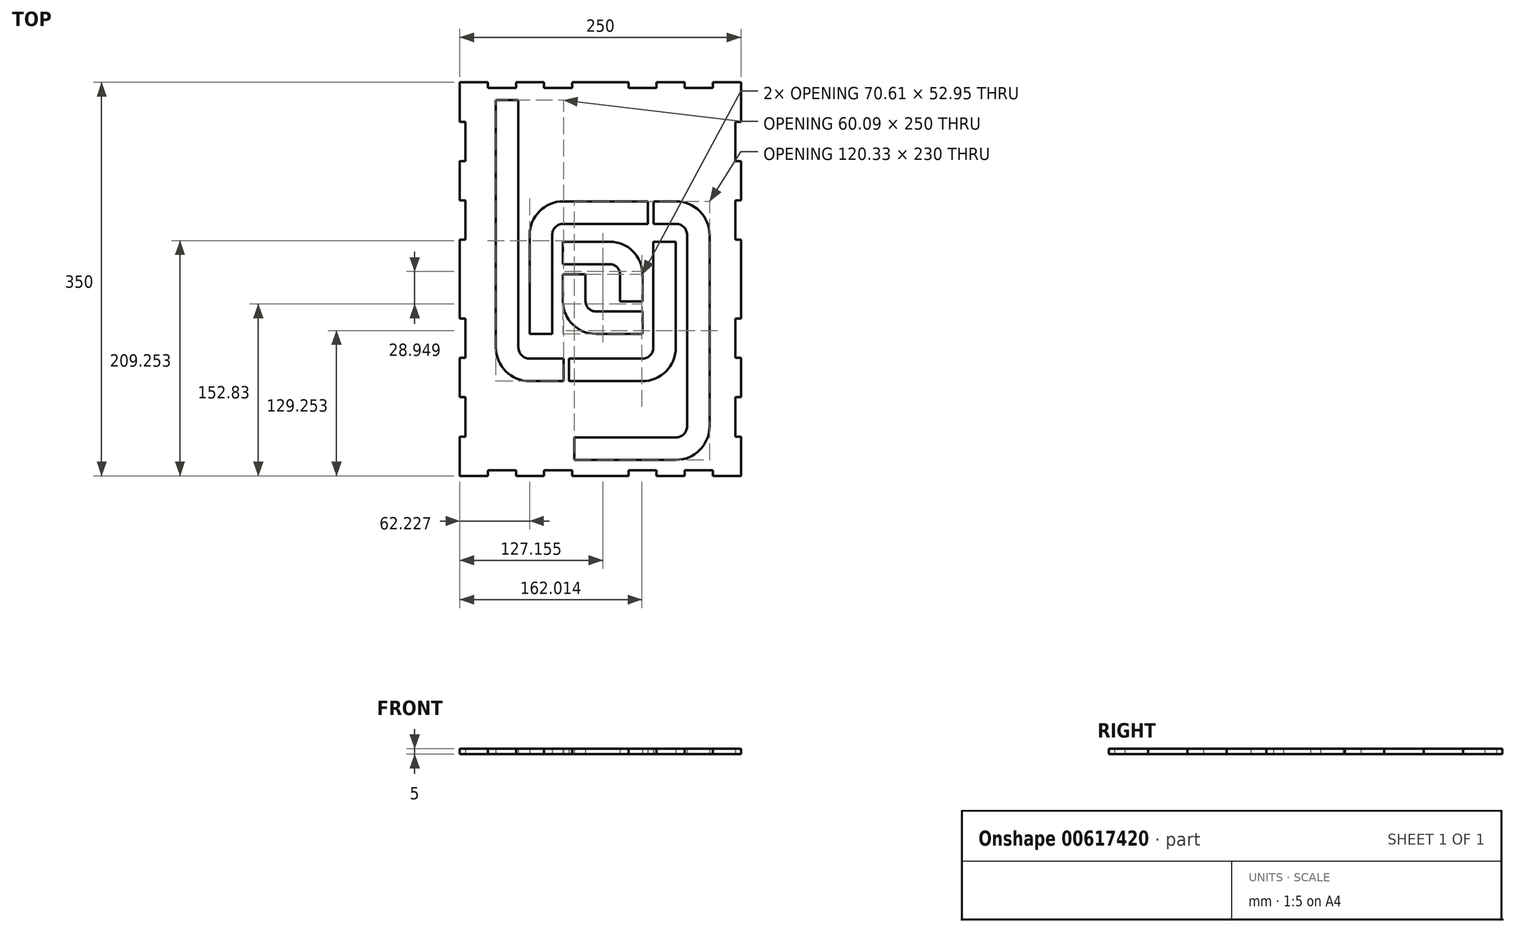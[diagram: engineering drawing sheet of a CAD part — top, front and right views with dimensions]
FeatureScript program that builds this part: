
annotation { "Feature Type Name" : "Feature", "Feature Type Description" : "" }
export const myFeature = defineFeature(function(context is Context, id is Id, definition is map)
    precondition{}
    {
        {
            var Q0;
            Q0=qCreatedBy(makeId("Top.planeOp"),FACE);
            var sketch = newSketch(context, id + "F0", { "sketchPlane" : qUnion([Q0])});
            skLineSegment(sketch, "E0.bottom", {"start": v(43.34, -187.45) * mm, "end": v(18.34, -187.45) * mm});
            skLineSegment(sketch, "E0.left", {"start": v(43.34, -187.45) * mm, "end": v(43.34, -152.45) * mm});
            skLineSegment(sketch, "E0.right", {"start": v(-206.66, -187.45) * mm, "end": v(-206.66, -152.45) * mm});
            skPoint(sketch, "E0.middle", {"position": v(-81.66, -12.45) * mm});
            skLineSegment(sketch, "E1", {"start": v(-81.66, -12.45) * mm, "end": v(-81.66, 157.55) * mm, "construction": true});
            skLineSegment(sketch, "E2", {"start": v(-206.66, -12.45) * mm, "end": v(-206.66, 22.55) * mm});
            skLineSegment(sketch, "E3", {"start": v(-81.66, 162.55) * mm, "end": v(-106.66, 162.55) * mm});
            skLineSegment(sketch, "E4", {"start": v(-181.66, 162.55) * mm, "end": v(-181.66, 157.55) * mm});
            skLineSegment(sketch, "E5", {"start": v(-181.66, 157.55) * mm, "end": v(-156.66, 157.55) * mm});
            skLineSegment(sketch, "E6", {"start": v(-156.66, 157.55) * mm, "end": v(-156.66, 162.55) * mm});
            skLineSegment(sketch, "E7", {"start": v(-181.66, 162.55) * mm, "end": v(-206.66, 162.55) * mm});
            skLineSegment(sketch, "E8.1.0.2", {"start": v(-156.66, 162.55) * mm, "end": v(-156.66, 157.55) * mm});
            skLineSegment(sketch, "E8.1.0.3", {"start": v(-131.66, 157.55) * mm, "end": v(-131.66, 162.55) * mm});
            skLineSegment(sketch, "E8.2.0.0", {"start": v(-131.66, 162.55) * mm, "end": v(-156.66, 162.55) * mm});
            skLineSegment(sketch, "E8.2.0.1", {"start": v(-131.66, 157.55) * mm, "end": v(-106.66, 157.55) * mm});
            skLineSegment(sketch, "E8.2.0.2", {"start": v(-131.66, 162.55) * mm, "end": v(-131.66, 157.55) * mm});
            skLineSegment(sketch, "E8.2.0.3", {"start": v(-106.66, 157.55) * mm, "end": v(-106.66, 162.55) * mm});
            skLineSegment(sketch, "E8.3.0.2", {"start": v(-106.66, 162.55) * mm, "end": v(-106.66, 157.55) * mm});
            skLineSegment(sketch, "E8.4.0.3", {"start": v(-56.66, 157.55) * mm, "end": v(-56.66, 162.55) * mm});
            skLineSegment(sketch, "E8.direction1", {"start": v(-206.66, 162.55) * mm, "end": v(-181.66, 162.55) * mm, "construction": true});
            skLineSegment(sketch, "E9.0.5.0", {"start": v(-56.66, 162.55) * mm, "end": v(-81.66, 162.55) * mm});
            skLineSegment(sketch, "E9.3.5.0", {"start": v(-56.66, 157.55) * mm, "end": v(-31.66, 157.55) * mm});
            skLineSegment(sketch, "E9.6.5.0", {"start": v(-56.66, 162.55) * mm, "end": v(-56.66, 157.55) * mm});
            skLineSegment(sketch, "E9.9.5.0", {"start": v(-31.66, 157.55) * mm, "end": v(-31.66, 162.55) * mm});
            skLineSegment(sketch, "E9.6.6.0", {"start": v(-31.66, 162.55) * mm, "end": v(-31.66, 157.55) * mm});
            skLineSegment(sketch, "E9.9.6.0", {"start": v(-6.66, 157.55) * mm, "end": v(-6.66, 162.55) * mm});
            skLineSegment(sketch, "E9.0.7.0", {"start": v(-6.66, 162.55) * mm, "end": v(-31.66, 162.55) * mm});
            skLineSegment(sketch, "E9.3.7.0", {"start": v(-6.66, 157.55) * mm, "end": v(18.34, 157.55) * mm});
            skLineSegment(sketch, "E9.6.7.0", {"start": v(-6.66, 162.55) * mm, "end": v(-6.66, 157.55) * mm});
            skLineSegment(sketch, "E9.9.7.0", {"start": v(18.34, 157.55) * mm, "end": v(18.34, 162.55) * mm});
            skLineSegment(sketch, "E9.6.8.0", {"start": v(18.34, 162.55) * mm, "end": v(18.34, 157.55) * mm});
            skLineSegment(sketch, "E9.9.8.0", {"start": v(43.34, 157.55) * mm, "end": v(43.34, 162.55) * mm});
            skLineSegment(sketch, "E10", {"start": v(-206.66, 162.55) * mm, "end": v(-181.66, 162.55) * mm});
            skLineSegment(sketch, "E11", {"start": v(-181.66, -187.45) * mm, "end": v(-206.66, -187.45) * mm});
            skLineSegment(sketch, "E12", {"start": v(-181.66, -182.45) * mm, "end": v(-181.66, -187.45) * mm});
            skLineSegment(sketch, "E13", {"start": v(-181.66, -182.45) * mm, "end": v(-156.66, -182.45) * mm});
            skLineSegment(sketch, "E14", {"start": v(-156.66, -187.45) * mm, "end": v(-156.66, -182.45) * mm});
            skLineSegment(sketch, "E15.1.0.1", {"start": v(-156.66, -182.45) * mm, "end": v(-156.66, -187.45) * mm});
            skLineSegment(sketch, "E15.1.0.3", {"start": v(-131.66, -187.45) * mm, "end": v(-131.66, -182.45) * mm});
            skLineSegment(sketch, "E15.2.0.0", {"start": v(-131.66, -187.45) * mm, "end": v(-156.66, -187.45) * mm});
            skLineSegment(sketch, "E15.2.0.1", {"start": v(-131.66, -182.45) * mm, "end": v(-131.66, -187.45) * mm});
            skLineSegment(sketch, "E15.2.0.2", {"start": v(-131.66, -182.45) * mm, "end": v(-106.66, -182.45) * mm});
            skLineSegment(sketch, "E15.2.0.3", {"start": v(-106.66, -187.45) * mm, "end": v(-106.66, -182.45) * mm});
            skLineSegment(sketch, "E15.3.0.1", {"start": v(-106.66, -182.45) * mm, "end": v(-106.66, -187.45) * mm});
            skLineSegment(sketch, "E15.4.0.0", {"start": v(-81.66, -187.45) * mm, "end": v(-106.66, -187.45) * mm});
            skLineSegment(sketch, "E15.4.0.3", {"start": v(-56.66, -187.45) * mm, "end": v(-56.66, -182.45) * mm});
            skLineSegment(sketch, "E15.5.0.0", {"start": v(-56.66, -187.45) * mm, "end": v(-81.66, -187.45) * mm});
            skLineSegment(sketch, "E15.5.0.1", {"start": v(-56.66, -182.45) * mm, "end": v(-56.66, -187.45) * mm});
            skLineSegment(sketch, "E15.5.0.2", {"start": v(-56.66, -182.45) * mm, "end": v(-31.66, -182.45) * mm});
            skLineSegment(sketch, "E15.5.0.3", {"start": v(-31.66, -187.45) * mm, "end": v(-31.66, -182.45) * mm});
            skLineSegment(sketch, "E15.6.0.1", {"start": v(-31.66, -182.45) * mm, "end": v(-31.66, -187.45) * mm});
            skLineSegment(sketch, "E15.6.0.3", {"start": v(-6.66, -187.45) * mm, "end": v(-6.66, -182.45) * mm});
            skLineSegment(sketch, "E15.7.0.0", {"start": v(-6.66, -187.45) * mm, "end": v(-31.66, -187.45) * mm});
            skLineSegment(sketch, "E15.7.0.1", {"start": v(-6.66, -182.45) * mm, "end": v(-6.66, -187.45) * mm});
            skLineSegment(sketch, "E15.7.0.2", {"start": v(-6.66, -182.45) * mm, "end": v(18.34, -182.45) * mm});
            skLineSegment(sketch, "E15.7.0.3", {"start": v(18.34, -187.45) * mm, "end": v(18.34, -182.45) * mm});
            skLineSegment(sketch, "E15.8.0.1", {"start": v(18.34, -182.45) * mm, "end": v(18.34, -187.45) * mm});
            skLineSegment(sketch, "E15.8.0.3", {"start": v(43.34, -187.45) * mm, "end": v(43.34, -182.45) * mm});
            skLineSegment(sketch, "E15.direction1", {"start": v(-206.66, -187.45) * mm, "end": v(-181.66, -187.45) * mm, "construction": true});
            skLineSegment(sketch, "E16", {"start": v(43.34, 127.55) * mm, "end": v(43.34, 162.55) * mm});
            skLineSegment(sketch, "E17", {"start": v(43.34, 127.55) * mm, "end": v(38.34, 127.55) * mm});
            skLineSegment(sketch, "E18", {"start": v(38.34, 127.55) * mm, "end": v(38.34, 92.55) * mm});
            skLineSegment(sketch, "E19", {"start": v(38.34, 92.55) * mm, "end": v(43.34, 92.55) * mm});
            skLineSegment(sketch, "E20.0.1.0", {"start": v(43.34, 92.55) * mm, "end": v(38.34, 92.55) * mm});
            skLineSegment(sketch, "E20.0.1.2", {"start": v(38.34, 57.55) * mm, "end": v(43.34, 57.55) * mm});
            skLineSegment(sketch, "E20.0.2.0", {"start": v(43.34, 57.55) * mm, "end": v(38.34, 57.55) * mm});
            skLineSegment(sketch, "E20.0.2.1", {"start": v(38.34, 57.55) * mm, "end": v(38.34, 22.55) * mm});
            skLineSegment(sketch, "E20.0.2.2", {"start": v(38.34, 22.55) * mm, "end": v(43.34, 22.55) * mm});
            skLineSegment(sketch, "E20.0.3.0", {"start": v(43.34, 22.55) * mm, "end": v(38.34, 22.55) * mm});
            skLineSegment(sketch, "E20.0.4.2", {"start": v(38.34, -47.45) * mm, "end": v(43.34, -47.45) * mm});
            skLineSegment(sketch, "E20.0.5.0", {"start": v(43.34, -47.45) * mm, "end": v(38.34, -47.45) * mm});
            skLineSegment(sketch, "E20.0.5.1", {"start": v(38.34, -47.45) * mm, "end": v(38.34, -82.45) * mm});
            skLineSegment(sketch, "E20.0.5.2", {"start": v(38.34, -82.45) * mm, "end": v(43.34, -82.45) * mm});
            skLineSegment(sketch, "E20.0.6.0", {"start": v(43.34, -82.45) * mm, "end": v(38.34, -82.45) * mm});
            skLineSegment(sketch, "E20.0.6.2", {"start": v(38.34, -117.45) * mm, "end": v(43.34, -117.45) * mm});
            skLineSegment(sketch, "E20.0.7.0", {"start": v(43.34, -117.45) * mm, "end": v(38.34, -117.45) * mm});
            skLineSegment(sketch, "E20.0.7.1", {"start": v(38.34, -117.45) * mm, "end": v(38.34, -152.45) * mm});
            skLineSegment(sketch, "E20.0.7.2", {"start": v(38.34, -152.45) * mm, "end": v(43.34, -152.45) * mm});
            skLineSegment(sketch, "E20.0.8.0", {"start": v(43.34, -152.45) * mm, "end": v(38.34, -152.45) * mm});
            skLineSegment(sketch, "E20.0.8.2", {"start": v(38.34, -187.45) * mm, "end": v(43.34, -187.45) * mm});
            skLineSegment(sketch, "E21", {"start": v(-206.66, 127.55) * mm, "end": v(-206.66, 162.55) * mm});
            skLineSegment(sketch, "E22", {"start": v(-206.66, 127.55) * mm, "end": v(-201.66, 127.55) * mm});
            skLineSegment(sketch, "E23", {"start": v(-201.66, 127.55) * mm, "end": v(-201.66, 92.55) * mm});
            skLineSegment(sketch, "E24", {"start": v(-201.66, 92.55) * mm, "end": v(-206.66, 92.55) * mm});
            skLineSegment(sketch, "E25.0.1.0", {"start": v(-206.66, 92.55) * mm, "end": v(-201.66, 92.55) * mm});
            skLineSegment(sketch, "E25.0.1.2", {"start": v(-201.66, 57.55) * mm, "end": v(-206.66, 57.55) * mm});
            skLineSegment(sketch, "E25.0.2.0", {"start": v(-206.66, 57.55) * mm, "end": v(-201.66, 57.55) * mm});
            skLineSegment(sketch, "E25.0.2.1", {"start": v(-201.66, 57.55) * mm, "end": v(-201.66, 22.55) * mm});
            skLineSegment(sketch, "E25.0.2.2", {"start": v(-201.66, 22.55) * mm, "end": v(-206.66, 22.55) * mm});
            skLineSegment(sketch, "E25.0.3.0", {"start": v(-206.66, 22.55) * mm, "end": v(-201.66, 22.55) * mm});
            skLineSegment(sketch, "E25.0.4.2", {"start": v(-201.66, -47.45) * mm, "end": v(-206.66, -47.45) * mm});
            skLineSegment(sketch, "E25.0.5.0", {"start": v(-206.66, -47.45) * mm, "end": v(-201.66, -47.45) * mm});
            skLineSegment(sketch, "E25.0.5.1", {"start": v(-201.66, -47.45) * mm, "end": v(-201.66, -82.45) * mm});
            skLineSegment(sketch, "E25.0.5.2", {"start": v(-201.66, -82.45) * mm, "end": v(-206.66, -82.45) * mm});
            skLineSegment(sketch, "E25.0.6.0", {"start": v(-206.66, -82.45) * mm, "end": v(-201.66, -82.45) * mm});
            skLineSegment(sketch, "E25.0.6.2", {"start": v(-201.66, -117.45) * mm, "end": v(-206.66, -117.45) * mm});
            skLineSegment(sketch, "E25.0.7.0", {"start": v(-206.66, -117.45) * mm, "end": v(-201.66, -117.45) * mm});
            skLineSegment(sketch, "E25.0.7.1", {"start": v(-201.66, -117.45) * mm, "end": v(-201.66, -152.45) * mm});
            skLineSegment(sketch, "E25.0.7.2", {"start": v(-201.66, -152.45) * mm, "end": v(-206.66, -152.45) * mm});
            skLineSegment(sketch, "E25.0.8.0", {"start": v(-206.66, -152.45) * mm, "end": v(-201.66, -152.45) * mm});
            skLineSegment(sketch, "E25.0.8.2", {"start": v(-201.66, -187.45) * mm, "end": v(-206.66, -187.45) * mm});
            skLineSegment(sketch, "E25.direction1", {"start": v(-206.66, 92.55) * mm, "end": v(-181.66, 92.55) * mm, "construction": true});
            skLineSegment(sketch, "E25.direction2", {"start": v(-206.66, 92.55) * mm, "end": v(-206.66, 57.55) * mm, "construction": true});
            skLineSegment(sketch, "E26", {"start": v(43.34, 92.55) * mm, "end": v(43.34, 57.55) * mm});
            skLineSegment(sketch, "E27", {"start": v(43.34, 22.55) * mm, "end": v(43.34, -47.45) * mm});
            skLineSegment(sketch, "E28", {"start": v(43.34, -82.45) * mm, "end": v(43.34, -117.45) * mm});
            skLineSegment(sketch, "E29.trimOffspring", {"start": v(-206.66, -47.45) * mm, "end": v(-206.66, -12.45) * mm});
            skLineSegment(sketch, "E30.trimOffspring", {"start": v(-206.66, -117.45) * mm, "end": v(-206.66, -82.45) * mm});
            skLineSegment(sketch, "E31.trimOffspring", {"start": v(-206.66, 57.55) * mm, "end": v(-206.66, 92.55) * mm});
            skLineSegment(sketch, "E32.trimOffspring", {"start": v(-81.66, 162.55) * mm, "end": v(-81.66, 212.55) * mm, "construction": true});
            skLineSegment(sketch, "E33", {"start": v(43.34, 162.55) * mm, "end": v(18.34, 162.55) * mm});
            skPoint(sketch, "E34.start.orphan", {"position": v(-206.66, 162.55) * mm});
            skPoint(sketch, "E35.startSnap0", {"position": v(87.85, 55.37) * mm});
            skArc(sketch, "E36", {"start": v(-154.48, -73.2) * mm, "mid": v(-151.55, -80.27) * mm, "end": v(-144.48, -83.2) * mm});
            skArc(sketch, "E37", {"start": v(-114.48, 36.8) * mm, "mid": v(-121.55, 33.87) * mm, "end": v(-124.48, 26.8) * mm});
            skArc(sketch, "E38", {"start": v(-94.81, -32.15) * mm, "mid": v(-92.2, -38.47) * mm, "end": v(-85.86, -41.1) * mm});
            skArc(sketch, "E39", {"start": v(-44.48, -83.2) * mm, "mid": v(-37.4, -80.27) * mm, "end": v(-34.48, -73.2) * mm});
            skArc(sketch, "E40", {"start": v(-4.48, 26.8) * mm, "mid": v(-7.4, 33.87) * mm, "end": v(-14.48, 36.8) * mm});
            skLineSegment(sketch, "E41", {"start": v(-4.48, 26.8) * mm, "end": v(-4.48, -143.2) * mm});
            skArc(sketch, "E42", {"start": v(-14.48, -153.2) * mm, "mid": v(-7.4, -150.27) * mm, "end": v(-4.48, -143.2) * mm});
            skLineSegment(sketch, "E43", {"start": v(-64.2, -32.15) * mm, "end": v(-64.2, -8.15) * mm});
            skArc(sketch, "E44", {"start": v(-64.2, -8.15) * mm, "mid": v(-66.82, -1.82) * mm, "end": v(-73.15, 0.8) * mm});
            skLineSegment(sketch, "E45", {"start": v(-44.2, -8.15) * mm, "end": v(-44.2, -32.15) * mm});
            skArc(sketch, "E46", {"start": v(-44.2, -8.15) * mm, "mid": v(-52.68, 12.32) * mm, "end": v(-73.15, 20.8) * mm});
            skLineSegment(sketch, "E47", {"start": v(-114.81, -32.15) * mm, "end": v(-114.81, -8.15) * mm});
            skArc(sketch, "E48", {"start": v(-114.81, -32.15) * mm, "mid": v(-106.33, -52.62) * mm, "end": v(-85.86, -61.1) * mm});
            skArc(sketch, "E49", {"start": v(-114.48, 56.8) * mm, "mid": v(-135.7, 48.02) * mm, "end": v(-144.48, 26.8) * mm});
            skArc(sketch, "E50", {"start": v(15.52, 26.8) * mm, "mid": v(6.73, 48.02) * mm, "end": v(-14.48, 56.8) * mm});
            skArc(sketch, "E51", {"start": v(-44.48, -103.2) * mm, "mid": v(-23.27, -94.41) * mm, "end": v(-14.48, -73.2) * mm});
            skLineSegment(sketch, "E52", {"start": v(15.52, -143.2) * mm, "end": v(15.52, 26.8) * mm});
            skArc(sketch, "E53", {"start": v(-14.48, -173.2) * mm, "mid": v(6.73, -164.41) * mm, "end": v(15.52, -143.2) * mm});
            skArc(sketch, "E54", {"start": v(-174.48, -73.2) * mm, "mid": v(-165.7, -94.41) * mm, "end": v(-144.48, -103.2) * mm});
            skLineSegment(sketch, "E55", {"start": v(-154.48, -73.2) * mm, "end": v(-154.48, 146.8) * mm});
            skLineSegment(sketch, "E56", {"start": v(-144.48, -61.1) * mm, "end": v(-144.48, 26.8) * mm});
            skLineSegment(sketch, "E57", {"start": v(-124.48, -61.1) * mm, "end": v(-124.48, 26.8) * mm});
            skLineSegment(sketch, "E58", {"start": v(-124.48, -61.1) * mm, "end": v(-144.48, -61.1) * mm});
            skLineSegment(sketch, "E59", {"start": v(-73.15, 0.8) * mm, "end": v(-114.81, 0.8) * mm});
            skLineSegment(sketch, "E60", {"start": v(-114.81, 0.8) * mm, "end": v(-114.81, 20.8) * mm});
            skLineSegment(sketch, "E61", {"start": v(-114.81, 20.8) * mm, "end": v(-73.15, 20.8) * mm});
            skLineSegment(sketch, "E62", {"start": v(-44.2, -61.1) * mm, "end": v(-85.86, -61.1) * mm});
            skLineSegment(sketch, "E63", {"start": v(-44.2, -41.1) * mm, "end": v(-44.2, -61.1) * mm});
            skLineSegment(sketch, "E64", {"start": v(-85.86, -41.1) * mm, "end": v(-44.2, -41.1) * mm});
            skLineSegment(sketch, "E65", {"start": v(-34.48, 20.8) * mm, "end": v(-34.48, -73.2) * mm});
            skLineSegment(sketch, "E66", {"start": v(-14.48, 20.8) * mm, "end": v(-34.48, 20.8) * mm});
            skLineSegment(sketch, "E67", {"start": v(-14.48, 20.8) * mm, "end": v(-14.48, -73.2) * mm});
            skLineSegment(sketch, "E68", {"start": v(-14.48, -153.2) * mm, "end": v(-104.81, -153.2) * mm});
            skLineSegment(sketch, "E69", {"start": v(-104.81, -153.2) * mm, "end": v(-104.81, -173.2) * mm});
            skLineSegment(sketch, "E70", {"start": v(-104.81, -173.2) * mm, "end": v(-14.48, -173.2) * mm});
            skLineSegment(sketch, "E71", {"start": v(-64.2, -32.15) * mm, "end": v(-44.2, -32.15) * mm});
            skLineSegment(sketch, "E72", {"start": v(-114.81, -8.15) * mm, "end": v(-94.81, -8.15) * mm});
            skLineSegment(sketch, "E73", {"start": v(-174.48, -73.2) * mm, "end": v(-174.48, 146.8) * mm});
            skLineSegment(sketch, "E74", {"start": v(-174.48, 146.8) * mm, "end": v(-154.48, 146.8) * mm});
            skLineSegment(sketch, "E75", {"start": v(-164.48, 103.44) * mm, "end": v(-164.48, -73.2) * mm, "construction": true});
            skLineSegment(sketch, "E76", {"start": v(-134.48, -61.1) * mm, "end": v(-134.48, 26.25) * mm, "construction": true});
            skLineSegment(sketch, "E77", {"start": v(-24.48, 30.23) * mm, "end": v(-24.48, -73.2) * mm, "construction": true});
            skLineSegment(sketch, "E78", {"start": v(51.19, -51.1) * mm, "end": v(-85.86, -51.1) * mm, "construction": true});
            skLineSegment(sketch, "E79", {"start": v(-54.15, -32.15) * mm, "end": v(-54.15, -8.15) * mm, "construction": true});
            skLineSegment(sketch, "E80", {"start": v(-104.81, -163.2) * mm, "end": v(46.2, -163.2) * mm, "construction": true});
            skLineSegment(sketch, "E81", {"start": v(-114.48, 46.8) * mm, "end": v(-14.48, 46.8) * mm, "construction": true});
            skLineSegment(sketch, "E82", {"start": v(-104.81, 28.69) * mm, "end": v(-104.81, -32.15) * mm, "construction": true});
            skLineSegment(sketch, "E83", {"start": v(-44.48, -93.2) * mm, "end": v(-144.48, -93.2) * mm, "construction": true});
            skLineSegment(sketch, "E84", {"start": v(5.52, 26.8) * mm, "end": v(5.52, -143.2) * mm, "construction": true});
            skArc(sketch, "E85.filletArc", {"start": v(-54.15, -8.15) * mm, "mid": v(-60.21, 5.77) * mm, "end": v(-74.54, 10.8) * mm, "construction": true});
            skArc(sketch, "E86.filletArc", {"start": v(-104.81, -32.15) * mm, "mid": v(-99.26, -45.54) * mm, "end": v(-85.86, -51.1) * mm, "construction": true});
            skArc(sketch, "E87.filletArc", {"start": v(-114.48, 46.8) * mm, "mid": v(-128.62, 40.95) * mm, "end": v(-134.48, 26.8) * mm, "construction": true});
            skArc(sketch, "E88.filletArc", {"start": v(5.52, 26.8) * mm, "mid": v(-0.34, 40.95) * mm, "end": v(-14.48, 46.8) * mm, "construction": true});
            skArc(sketch, "E89.filletArc", {"start": v(-44.48, -93.2) * mm, "mid": v(-30.34, -87.34) * mm, "end": v(-24.48, -73.2) * mm, "construction": true});
            skArc(sketch, "E90.filletArc", {"start": v(-14.48, -163.2) * mm, "mid": v(-0.34, -157.34) * mm, "end": v(5.52, -143.2) * mm, "construction": true});
            skArc(sketch, "E91.filletArc", {"start": v(-164.48, -73.2) * mm, "mid": v(-158.62, -87.34) * mm, "end": v(-144.48, -93.2) * mm, "construction": true});
            skLineSegment(sketch, "E92", {"start": v(56.76, -23.2) * mm, "end": v(40.63, -23.2) * mm, "construction": true});
            skLineSegment(sketch, "E93", {"start": v(-79.48, 33.44) * mm, "end": v(-79.48, 18.26) * mm, "construction": true});
            skLineSegment(sketch, "E94", {"start": v(-114.39, -83.2) * mm, "end": v(-114.39, -103.2) * mm});
            skLineSegment(sketch, "E95", {"start": v(-109.39, -83.2) * mm, "end": v(-109.39, -103.2) * mm});
            skLineSegment(sketch, "E96.trimOffspring", {"start": v(-114.39, -83.2) * mm, "end": v(-144.48, -83.2) * mm});
            skLineSegment(sketch, "E97.trimOffspring", {"start": v(-114.39, -103.2) * mm, "end": v(-144.48, -103.2) * mm});
            skLineSegment(sketch, "E98.trimOffspring", {"start": v(-114.48, 36.8) * mm, "end": v(-39.41, 36.8) * mm});
            skLineSegment(sketch, "E99", {"start": v(-94.81, -32.15) * mm, "end": v(-94.81, -8.15) * mm});
            skLineSegment(sketch, "E100", {"start": v(-74.54, 10.8) * mm, "end": v(-263.7, 10.8) * mm, "construction": true});
            skLineSegment(sketch, "E101", {"start": v(-104.81, -1.73) * mm, "end": v(-104.81, 135.36) * mm, "construction": true});
            skLineSegment(sketch, "E102.trimOffspring", {"start": v(-44.48, -103.2) * mm, "end": v(-109.39, -103.2) * mm});
            skLineSegment(sketch, "E103.trimOffspring", {"start": v(-44.48, -83.2) * mm, "end": v(-109.39, -83.2) * mm});
            skLineSegment(sketch, "E104", {"start": v(-114.48, 56.8) * mm, "end": v(-39.41, 56.8) * mm});
            skLineSegment(sketch, "E105", {"start": v(-34.41, 56.8) * mm, "end": v(-14.48, 56.8) * mm});
            skLineSegment(sketch, "E106", {"start": v(-34.41, 56.8) * mm, "end": v(-34.41, 36.8) * mm});
            skLineSegment(sketch, "E107", {"start": v(-39.41, 56.8) * mm, "end": v(-39.41, 36.8) * mm});
            skLineSegment(sketch, "E108.trimOffspring", {"start": v(-34.41, 36.8) * mm, "end": v(-14.48, 36.8) * mm});
            skPoint(sketch, "E109.middle", {"position": v(-64.2, -8.15) * mm});
            skPoint(sketch, "E109.top.start.orphan", {"position": v(91.72, 229.16) * mm});
            skPoint(sketch, "E110.orphan", {"position": v(-220.12, 229.16) * mm});
            skPoint(sketch, "E109.bottom.end.orphan", {"position": v(-220.12, -245.45) * mm});
            skPoint(sketch, "E109.bottom.start.orphan", {"position": v(91.72, -245.45) * mm});
            skSolve(sketch);
        }
        {
            var Q0;
            Q0=makeQuery(id+"F0.imprint","IMPRINT",FACE,{"disambiguationData":[TD([[makeQuery(id+"F0.imprint","IMPRINT",EDGE,{"derivedFrom":sQuery(id+"F0.wireOp",EDGE,"E0.bottom")}),-1.0]])]});
            extrude(context, id + "F1", {"entities" : qUnion([Q0]), "depth" : 5 * mm, "offsetDistance" : 25 * mm});
        }
    });
